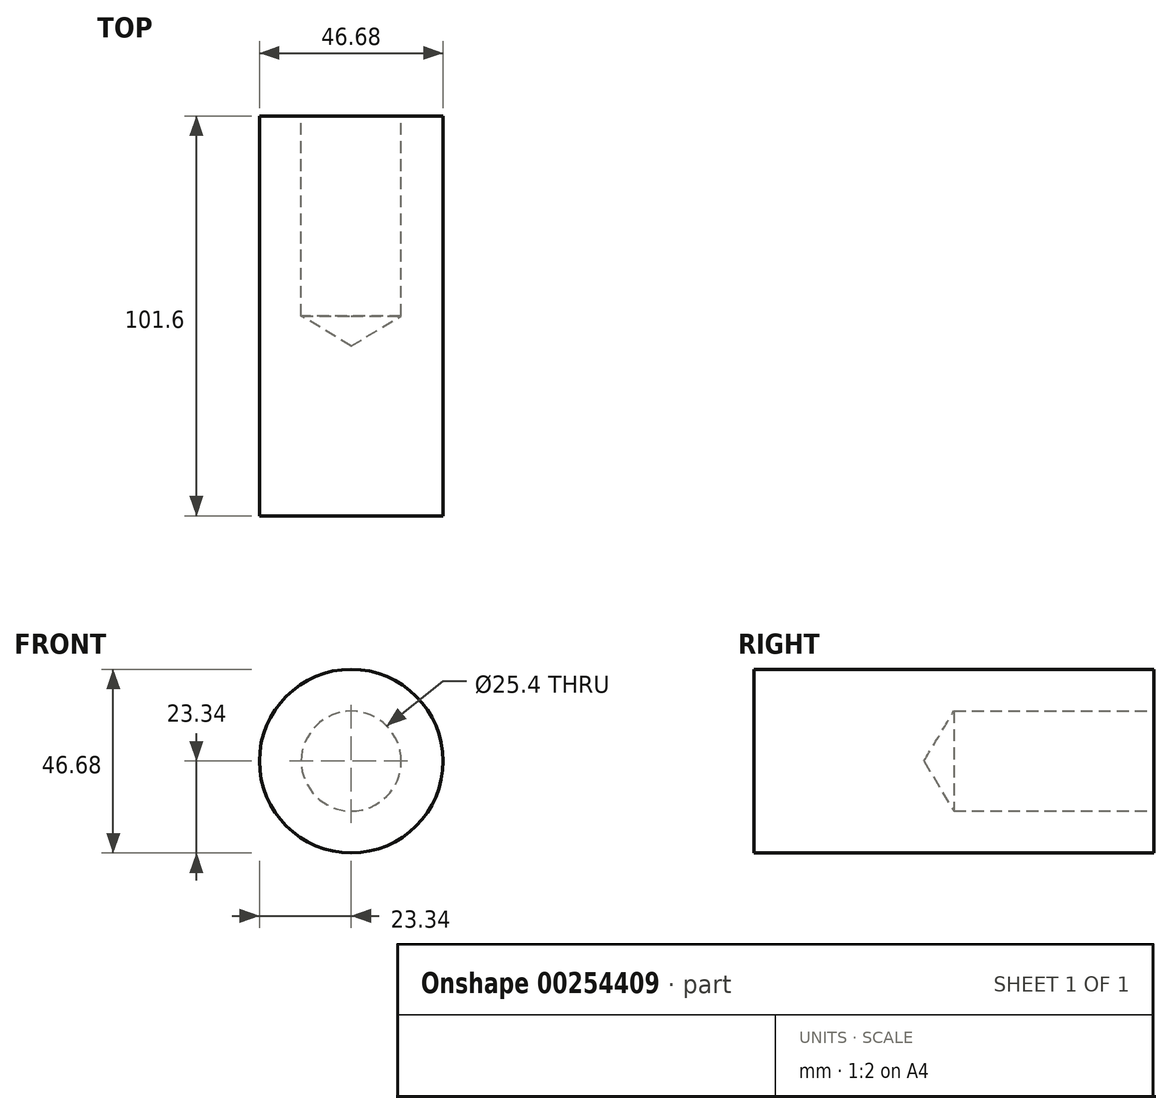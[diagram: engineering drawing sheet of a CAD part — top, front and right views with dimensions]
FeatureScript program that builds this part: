
annotation { "Feature Type Name" : "Feature", "Feature Type Description" : "" }
export const myFeature = defineFeature(function(context is Context, id is Id, definition is map)
    precondition{}
    {
        {
            var Q0;
            Q0=qCreatedBy(makeId("Front.planeOp"),FACE);
            var sketch = newSketch(context, id + "F0", { "sketchPlane" : qUnion([Q0])});
            skCircle(sketch, "E0", {"center": v(0, 0) * mm, "radius": 23.34 * mm});
            skSolve(sketch);
        }
        {
            var Q0;
            Q0 = qSketchRegion(id + "F0", true);
            extrude(context, id + "F1", {"entities" : qUnion([Q0]), "depth" : 101.6 * mm});
        }
        {
            var Q0;
            Q0=qCreatedBy(makeId("Front.planeOp"),FACE);
            var sketch = newSketch(context, id + "F2", { "sketchPlane" : qUnion([Q0])});
            skLineSegment(sketch, "E1.bottom", {"start": v(0, 0) * mm, "end": v(39.5, 0) * mm});
            skLineSegment(sketch, "E1.top", {"start": v(0, -46.03) * mm, "end": v(39.5, -46.03) * mm});
            skLineSegment(sketch, "E1.left", {"start": v(0, 0) * mm, "end": v(0, -46.03) * mm});
            skLineSegment(sketch, "E1.right", {"start": v(39.5, 0) * mm, "end": v(39.5, -46.03) * mm});
            skSolve(sketch);
        }
        {
            var Q0;
            Q0=sQuery(id+"F2.wireOp",VERTEX,"E1.bottom.start");
            var Q1;
            Q1=makeQuery(id+"F1.opExtrude","SWEPT_BODY",BODY,{"disambiguationData":[OSD([sQuery(id+"F0.wireOp",EDGE,"E0")])]});
            hole(context, id + "F3", {"style" : HoleStyle.SIMPLE, "endStyle" : HoleEndStyle.BLIND, "oppositeDirection" : true, "holeDiameter" : 25.4 * mm, "holeDepth" : 50.8 * mm, "tappedDepth" : 12.7 * mm, "tapClearance" : 3, "locations" : qUnion([Q0]), "scope" : qUnion([Q1])});
        }
    });
